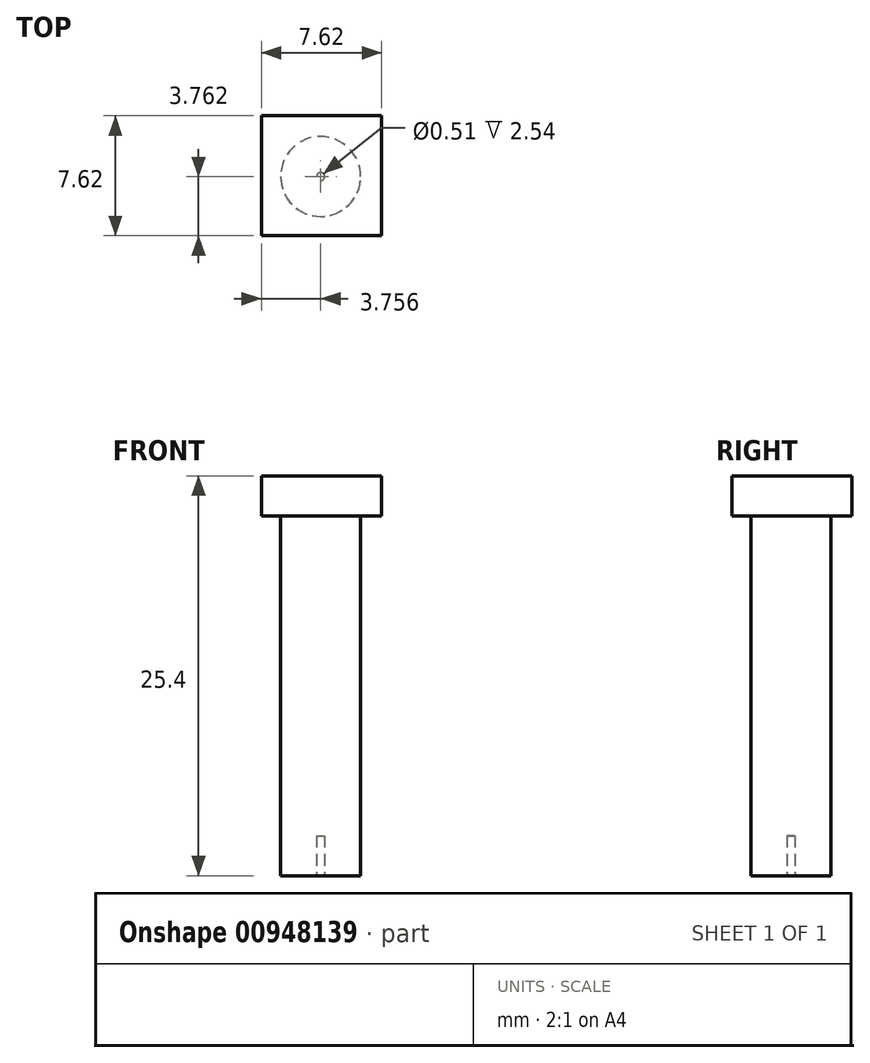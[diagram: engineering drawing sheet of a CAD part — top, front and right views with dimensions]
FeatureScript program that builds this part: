
annotation { "Feature Type Name" : "Feature", "Feature Type Description" : "" }
export const myFeature = defineFeature(function(context is Context, id is Id, definition is map)
    precondition{}
    {
        {
            var Q0;
            Q0=qCreatedBy(makeId("Top.planeOp"),FACE);
            var sketch = newSketch(context, id + "F0", { "sketchPlane" : qUnion([Q0])});
            skLineSegment(sketch, "E0.bottom", {"start": v(-42.6, -18.03) * mm, "end": v(-34.99, -18.03) * mm});
            skLineSegment(sketch, "E0.top", {"start": v(-42.6, -25.65) * mm, "end": v(-34.99, -25.65) * mm});
            skLineSegment(sketch, "E0.left", {"start": v(-42.6, -18.03) * mm, "end": v(-42.6, -25.65) * mm});
            skLineSegment(sketch, "E0.right", {"start": v(-34.99, -18.03) * mm, "end": v(-34.99, -25.65) * mm});
            skSolve(sketch);
        }
        {
            var Q0;
            Q0=qSketchRegion(id+"F0",true);
            var Q1;
            Q1=qSketchRegion(id+"F2",true);
            extrude(context, id + "F1", {"entities" : qUnion([Q0, Q1]), "depth" : 2.54 * mm, "offsetDistance" : 25.4 * mm});
        }
        {
            var Q0;
            Q0=makeQuery(id+"F1.opExtrude","CAP_FACE",FACE,{"disambiguationData":[OSD([sQuery(id+"F0.wireOp",EDGE,"E0.bottom"),sQuery(id+"F0.wireOp",EDGE,"E0.top"),sQuery(id+"F0.wireOp",EDGE,"E0.left"),sQuery(id+"F0.wireOp",EDGE,"E0.right")])],"isStart":true});
            var sketch = newSketch(context, id + "F2", { "sketchPlane" : qUnion([Q0])});
            skCircle(sketch, "E1", {"center": v(-38.85, 21.89) * mm, "radius": 2.54 * mm});
            skCircle(sketch, "E2", {"center": v(-38.85, 21.89) * mm, "radius": 1.27 * mm});
            skSolve(sketch);
        }
        {
            var Q0;
            Q0=makeQuery(id+"F2.imprint","IMPRINT",FACE,{"disambiguationData":[TD([[makeQuery(id+"F2.imprint","IMPRINT",EDGE,{"derivedFrom":sQuery(id+"F2.wireOp",EDGE,"E2")}),1.0]])]});
            extrude(context, id + "F3", {"entities" : qUnion([Q0]), "operationType" : NewBodyOperationType.ADD, "depth" : 22.86 * mm, "offsetDistance" : 25.4 * mm});
        }
        {
            var Q0;
            Q0=makeQuery(id+"F3.opExtrude","CAP_FACE",FACE,{"disambiguationData":[OSD([sQuery(id+"F2.wireOp",EDGE,"E2")])],"isStart":false});
            var sketch = newSketch(context, id + "F4", { "sketchPlane" : qUnion([Q0])});
            skCircle(sketch, "E3", {"center": v(-38.85, 21.89) * mm, "radius": 0.25 * mm});
            skSolve(sketch);
        }
        {
            var Q0;
            Q0=qSketchRegion(id+"F4",true);
            extrude(context, id + "F5", {"entities" : qUnion([Q0]), "operationType" : NewBodyOperationType.REMOVE, "oppositeDirection" : true, "depth" : 2.54 * mm, "offsetDistance" : 25.4 * mm});
        }
        {
            var Q0;
            Q0=qSketchRegion(id+"F2",true);
            extrude(context, id + "F6", {"entities" : qUnion([Q0]), "operationType" : NewBodyOperationType.ADD, "depth" : 22.86 * mm, "offsetDistance" : 25.4 * mm});
        }
    });
